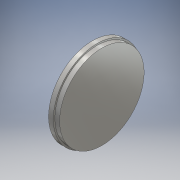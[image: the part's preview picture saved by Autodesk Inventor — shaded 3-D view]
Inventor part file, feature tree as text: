
AUTODESK INVENTOR PART (.ipt)
format: ipt  version: 2016 (Build 200138000, 138)  size: 202,752 bytes
history: native  units: mm
features: revolve x1, sketch x1
ambient origin geometry x8: Origin, YZ Plane, XZ Plane, XY Plane, X Axis, Y Axis, Z Axis, Center Point
bodies: Body1 (feature_tree)
feature tree (2):
  revolve  "Revolution2"  [1 undecoded]
  sketch  "Sketch1"  dims[d0=27.75mm d7=13.5mm d8=11.0mm d9=10.566406mm d10=1.0mm d11=3.0mm d12=3.0mm d14=16.2mm d15=2.5mm d16=1.5mm d17=1.0mm d18=1.5mm d19=1.5mm d20=90.0deg]
note: 1 required parameter value undecoded (feature->parameter linkage not recoverable at this tier; creation-order binding heuristic only, values carry confidence <= 0.55)
